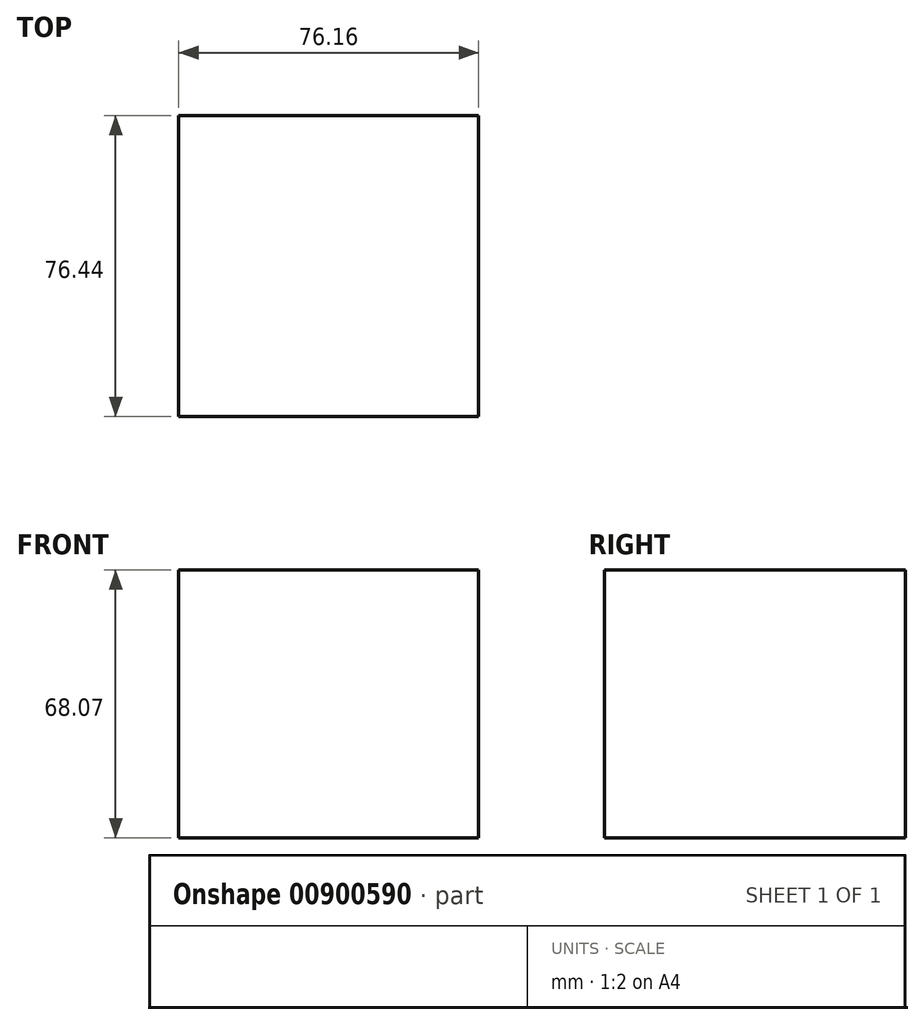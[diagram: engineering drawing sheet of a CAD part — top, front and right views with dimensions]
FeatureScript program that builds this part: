
annotation { "Feature Type Name" : "Feature", "Feature Type Description" : "" }
export const myFeature = defineFeature(function(context is Context, id is Id, definition is map)
    precondition{}
    {
        {
            var Q0;
            Q0=qCreatedBy(makeId("Top.planeOp"),FACE);
            var sketch = newSketch(context, id + "F0", { "sketchPlane" : qUnion([Q0])});
            skLineSegment(sketch, "E0.bottom", {"start": v(0, 0) * mm, "end": v(-76.16, 0) * mm});
            skLineSegment(sketch, "E0.top", {"start": v(0, -76.44) * mm, "end": v(-76.16, -76.44) * mm});
            skLineSegment(sketch, "E0.left", {"start": v(0, 0) * mm, "end": v(0, -76.44) * mm});
            skLineSegment(sketch, "E0.right", {"start": v(-76.16, 0) * mm, "end": v(-76.16, -76.44) * mm});
            skSolve(sketch);
        }
        {
            var Q0;
            Q0=makeQuery(id+"F0.imprint","IMPRINT",FACE,{"disambiguationData":[TD([[makeQuery(id+"F0.imprint","IMPRINT",EDGE,{"derivedFrom":sQuery(id+"F0.wireOp",EDGE,"E0.bottom")}),1.0]])]});
            extrude(context, id + "F1", {"entities" : qUnion([Q0]), "depth" : 68.07 * mm, "offsetDistance" : 25.4 * mm});
        }
    });
